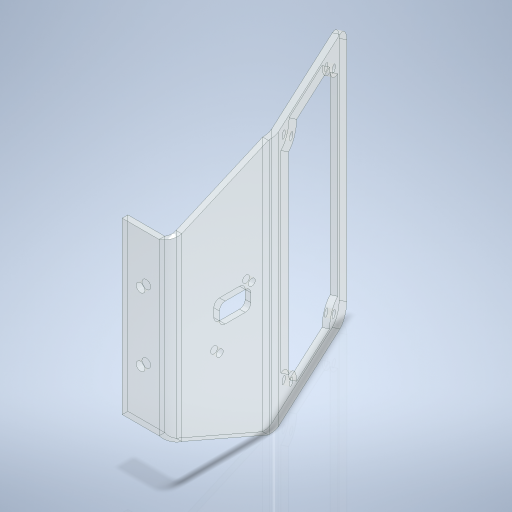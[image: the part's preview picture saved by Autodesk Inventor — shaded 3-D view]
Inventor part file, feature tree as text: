
AUTODESK INVENTOR PART (.ipt)
format: ipt  version: 2024 (Build 280153000, 153)  size: 389,632 bytes
history: native  units: mm
features: sketch x8, other x7, hole x3, extrude x1, fillet x1
ambient origin geometry x8: Origin, YZ Plane, XZ Plane, XY Plane, X Axis, Y Axis, Z Axis, Center Point
bodies: Volumenkörper1 (feature_tree)
feature tree (20):
  extrude  "Extrusion1"  Depth=2.0mm
  other  "Lasche1"
  hole  "Bohrung1"  [1 undecoded]
  fillet  "Rundung1"  Radius=50.0mm
  hole  "Bohrung2"  [1 undecoded]
  hole  "Bohrung3"  [1 undecoded]
  sketch  "Skizze1"  dims[d0=2.0mm d1=2.0mm]
  sketch  "Skizze3"  dims[d3=27.052603mm d4=10.0mm d5=50.0mm]
  other  "Grobblech1"
  other  "Biegung1"
  other  "Ecke1"
  sketch  "Skizze6"  dims[d6=4.363323mm d7=35.0mm]
  sketch  "Skizze7"  dims[d8=90.0mm d9=0.0mm d10=2.0mm]
  sketch  "Skizze9"  dims[d11=2.0mm]
  sketch  "Skizze11"  dims[d12=1.0mm]
  sketch  "Skizze12"  dims[d13=4.0mm]
  sketch  "Skizze13"  dims[d14=2.0mm d15=15.0mm d16=90.0deg d17=2.0mm d18=8.0mm d19=2.0mm d20=2.0mm d21=60.0mm d22=15.0mm d23=2.0mm d24=0.0mm d29=80.0mm d33=6.0mm d35=2.0mm d36=0.0mm d37=2.5mm d38=6.0mm d39=4.0mm d40=2.0mm d41=90.0deg d42=2.0mm d43=20.594885mm d44=75.0mm d46=5.0mm d47=3.1mm d48=6.0mm d49=4.0mm d50=2.0mm d51=90.0deg d52=8.0mm d53=20.594885mm d54=24.0mm d55=2.0mm d56=26.5mm d57=17.3mm d58=11.1mm d59=2.0mm d60=0.0mm d61=2.5mm d62=6.0mm d63=4.0mm d64=2.0mm d65=90.0deg d66=8.0mm d67=20.594885mm d68=15.98mm d70=28.7mm d71=17.38mm d72=20.31mm d74=31.0mm d75=75.0mm d77=36.0mm]
  other  "Ausschneiden1"
  other  "Ausschneiden2"
  other  "Ausschneiden3"
note: 3 required parameter values undecoded (feature->parameter linkage not recoverable at this tier; creation-order binding heuristic only, values carry confidence <= 0.55)
